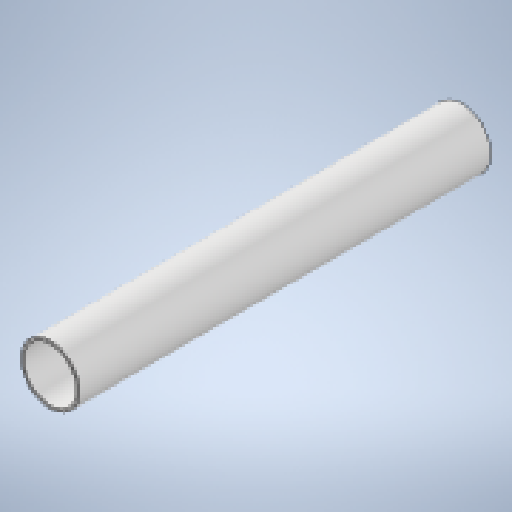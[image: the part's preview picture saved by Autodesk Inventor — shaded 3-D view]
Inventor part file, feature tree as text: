
AUTODESK INVENTOR PART (.ipt)
format: ipt  version: 2025.3 (Build 293356030, 356C)  size: 143,360 bytes
history: native  units: mm
features: extrude x1, sketch x1
ambient origin geometry x8: Origin, YZ Plane, XZ Plane, XY Plane, X Axis, Y Axis, Z Axis, Center Point
bodies: Solid1 (feature_tree)
feature tree (2):
  extrude  "Extrusion1"  Depth=442.0mm
  sketch  "Sketch1"  dims[d0=57.0mm d1=3.0mm d2=442.0mm d3=0.0mm]
